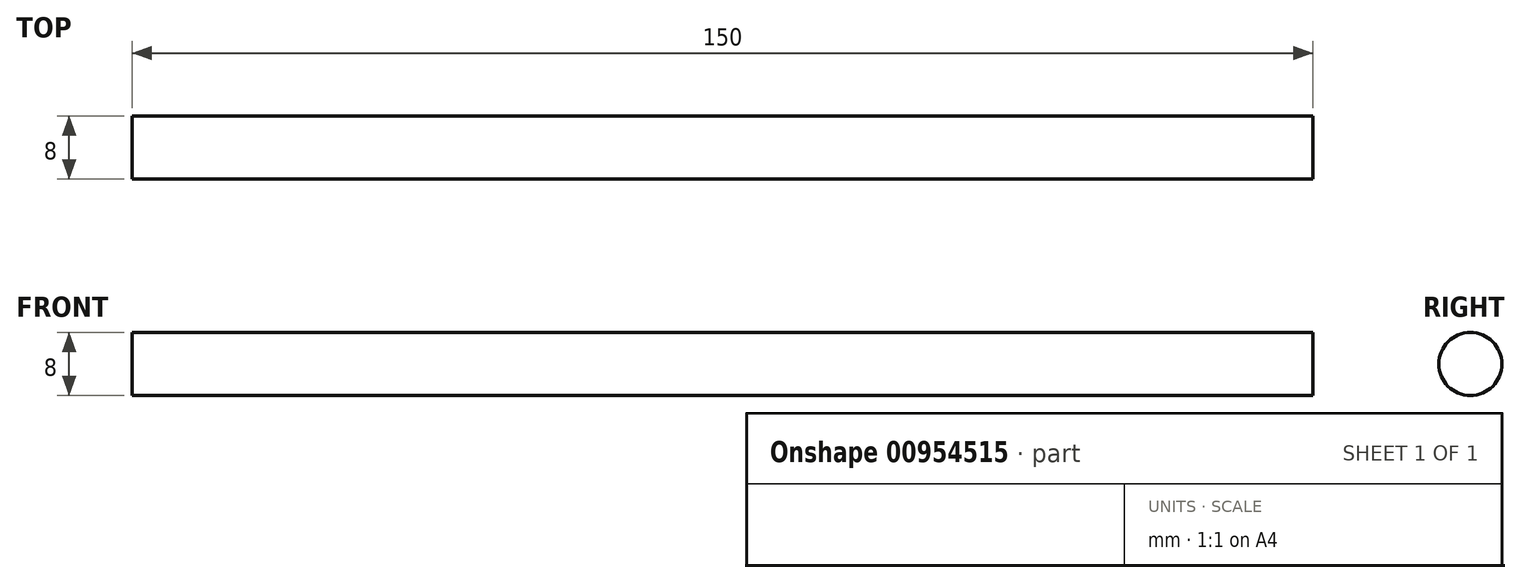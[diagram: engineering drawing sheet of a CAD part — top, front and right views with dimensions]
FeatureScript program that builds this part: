
annotation { "Feature Type Name" : "Feature", "Feature Type Description" : "" }
export const myFeature = defineFeature(function(context is Context, id is Id, definition is map)
    precondition{}
    {
        {
            var Q0;
            Q0=qCreatedBy(makeId("Right.planeOp"),FACE);
            var sketch = newSketch(context, id + "F0", { "sketchPlane" : qUnion([Q0])});
            skCircle(sketch, "E0", {"center": v(0, 0) * mm, "radius": 4 * mm});
            skSolve(sketch);
        }
        {
            var Q0;
            Q0=makeQuery(id+"F0.imprint","IMPRINT",FACE,{"disambiguationData":[TD([[makeQuery(id+"F0.imprint","IMPRINT",EDGE,{"derivedFrom":sQuery(id+"F0.wireOp",EDGE,"E0")}),1.0]])]});
            extrude(context, id + "F1", {"entities" : qUnion([Q0]), "depth" : 150 * mm, "offsetDistance" : 25 * mm});
        }
    });
